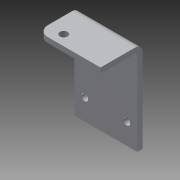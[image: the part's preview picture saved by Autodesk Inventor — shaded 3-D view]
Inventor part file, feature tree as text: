
AUTODESK INVENTOR PART (.ipt)
format: ipt  version: 2014 (Build 180170000, 170)  size: 119,808 bytes
history: native  units: in
note: dims shown in document units (in); Inventor stores cm internally (conversion verified against a paired STEP export)
features: sheet_metal_op x4, sketch x3, other x3
ambient origin geometry x8: Origin, YZ Plane, XZ Plane, XY Plane, X Axis, Y Axis, Z Axis, Center Point
bodies: Solid1 (feature_tree)
feature tree (10):
  sheet_metal_op  "Face1"
  sheet_metal_op  "Flange1"
  sketch  "Sketch1"  dims[d0=1.5in]
  other  "Plate1"
  sketch  "Sketch2"  dims[d1=2.0in]
  other  "Plate2"
  sheet_metal_op  "Bend1"
  sheet_metal_op  "Corner1"
  sketch  "Sketch4"  dims[d2=0.163in d3=0.25in d4=0.7874in d6=1.0in d7=0.3937in d9=1.0in d11=0.125in d12=0.125in d13=0.0625in d14=0.25in d15=0.125in d16=1.0in d17=90.0deg d18=0.05in d19=0.5in d20=0.125in d21=0.125in d22=0.5in d28=0.187in d29=0.25in d31=0.125in d32=0.0in d34=0.375in d35=0.25in]
  other  "Cut2"
